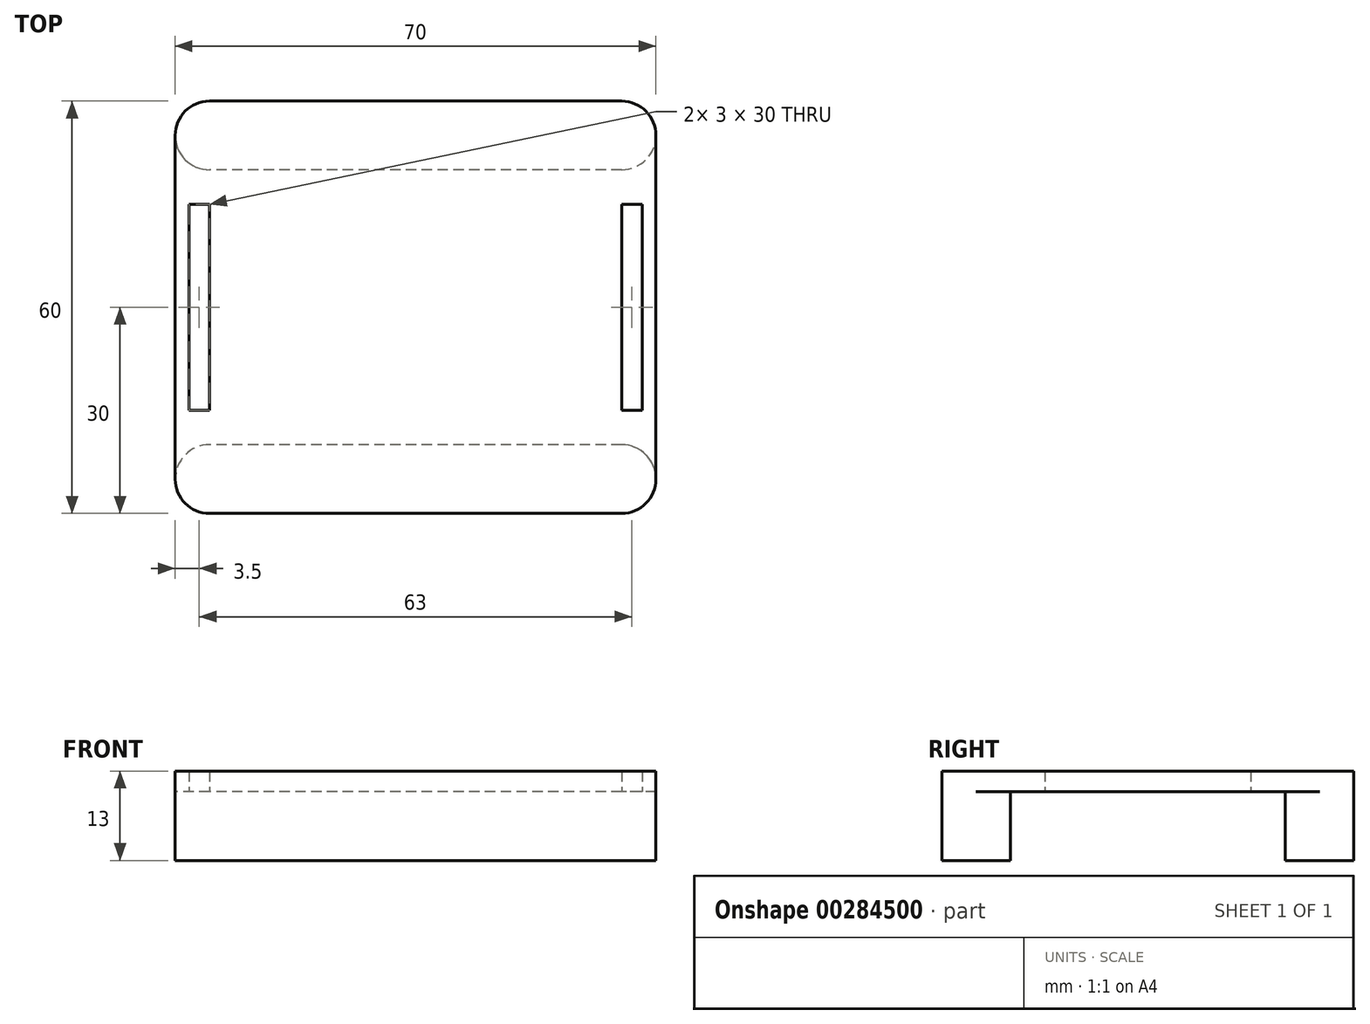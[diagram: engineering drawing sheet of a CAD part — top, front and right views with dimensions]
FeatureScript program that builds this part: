
annotation { "Feature Type Name" : "Feature", "Feature Type Description" : "" }
export const myFeature = defineFeature(function(context is Context, id is Id, definition is map)
    precondition{}
    {
        {
            var Q0;
            Q0=qCreatedBy(makeId("Top.planeOp"),FACE);
            var sketch = newSketch(context, id + "F0", { "sketchPlane" : qUnion([Q0])});
            skLineSegment(sketch, "E0.bottom", {"start": v(35, -30) * mm, "end": v(-35, -30) * mm});
            skLineSegment(sketch, "E0.top", {"start": v(35, 30) * mm, "end": v(-35, 30) * mm});
            skLineSegment(sketch, "E0.left", {"start": v(35, -30) * mm, "end": v(35, 30) * mm});
            skLineSegment(sketch, "E0.right", {"start": v(-35, -30) * mm, "end": v(-35, 30) * mm});
            skPoint(sketch, "E0.middle", {"position": v(0, 0) * mm});
            skSolve(sketch);
        }
        {
            var Q0;
            Q0 = qSketchRegion(id + "F0", true);
            extrude(context, id + "F1", {"entities" : qUnion([Q0]), "depth" : 3 * mm});
        }
        {
            var Q0;
            Q0=qCreatedBy(makeId("Top.planeOp"),FACE);
            var sketch = newSketch(context, id + "F2", { "sketchPlane" : qUnion([Q0])});
            skLineSegment(sketch, "E1.bottom", {"start": v(33, -15) * mm, "end": v(30, -15) * mm});
            skLineSegment(sketch, "E1.top", {"start": v(33, 15) * mm, "end": v(30, 15) * mm});
            skLineSegment(sketch, "E1.left", {"start": v(30, -15) * mm, "end": v(30, 15) * mm});
            skLineSegment(sketch, "E1.right", {"start": v(33, -15) * mm, "end": v(33, 15) * mm});
            skPoint(sketch, "E1.middle", {"position": v(31.5, 0) * mm});
            skLineSegment(sketch, "E2.bottom", {"start": v(-30, -15) * mm, "end": v(-33, -15) * mm});
            skLineSegment(sketch, "E2.top", {"start": v(-30, 15) * mm, "end": v(-33, 15) * mm});
            skLineSegment(sketch, "E2.left", {"start": v(-30, -15) * mm, "end": v(-30, 15) * mm});
            skLineSegment(sketch, "E2.right", {"start": v(-33, -15) * mm, "end": v(-33, 15) * mm});
            skPoint(sketch, "E2.middle", {"position": v(-31.5, 0) * mm});
            skSolve(sketch);
        }
        {
            var Q0;
            Q0 = qSketchRegion(id + "F2", true);
            extrude(context, id + "F3", {"entities" : qUnion([Q0]), "operationType" : NewBodyOperationType.REMOVE, "depth" : 25 * mm});
        }
        {
            var Q0;
            Q0=qCreatedBy(makeId("Top.planeOp"),FACE);
            var sketch = newSketch(context, id + "F4", { "sketchPlane" : qUnion([Q0])});
            skLineSegment(sketch, "E3.bottom", {"start": v(35, 20) * mm, "end": v(-35, 20) * mm});
            skLineSegment(sketch, "E3.top", {"start": v(35, 30) * mm, "end": v(-35, 30) * mm});
            skLineSegment(sketch, "E3.left", {"start": v(35, 20) * mm, "end": v(35, 30) * mm});
            skLineSegment(sketch, "E3.right", {"start": v(-35, 20) * mm, "end": v(-35, 30) * mm});
            skPoint(sketch, "E3.middle", {"position": v(0, 25) * mm});
            skLineSegment(sketch, "E4.bottom", {"start": v(35, -30) * mm, "end": v(-35, -30) * mm});
            skLineSegment(sketch, "E4.top", {"start": v(35, -20) * mm, "end": v(-35, -20) * mm});
            skLineSegment(sketch, "E4.left", {"start": v(35, -30) * mm, "end": v(35, -20) * mm});
            skLineSegment(sketch, "E4.right", {"start": v(-35, -30) * mm, "end": v(-35, -20) * mm});
            skPoint(sketch, "E4.middle", {"position": v(0, -25) * mm});
            skSolve(sketch);
        }
        {
            var Q0;
            Q0 = qSketchRegion(id + "F4", true);
            extrude(context, id + "F5", {"entities" : qUnion([Q0]), "operationType" : NewBodyOperationType.ADD, "oppositeDirection" : true, "depth" : 10 * mm});
        }
        {
            var Q0;
            Q0=makeQuery(id+"F5.boolean.opBoolean","MERGE",EDGE,{"derivedFrom":[makeQuery(id+"F1.opExtrude","SWEPT_EDGE",EDGE,{"disambiguationData":[OSD([sQuery(id+"F0.wireOp",EDGE,"E0.bottom"),sQuery(id+"F0.wireOp",EDGE,"E0.left")])]}),makeQuery(id+"F5.opExtrude","SWEPT_EDGE",EDGE,{"disambiguationData":[OSD([sQuery(id+"F4.wireOp",EDGE,"E4.bottom"),sQuery(id+"F4.wireOp",EDGE,"E4.left")])]})]});
            var Q1;
            Q1=makeQuery(id+"F5.boolean.opBoolean","MERGE",EDGE,{"derivedFrom":[makeQuery(id+"F1.opExtrude","SWEPT_EDGE",EDGE,{"disambiguationData":[OSD([sQuery(id+"F0.wireOp",EDGE,"E0.bottom"),sQuery(id+"F0.wireOp",EDGE,"E0.right")])]}),makeQuery(id+"F5.opExtrude","SWEPT_EDGE",EDGE,{"disambiguationData":[OSD([sQuery(id+"F4.wireOp",EDGE,"E4.bottom"),sQuery(id+"F4.wireOp",EDGE,"E4.right")])]})]});
            var Q2;
            Q2=makeQuery(id+"F5.opExtrude","SWEPT_EDGE",EDGE,{"disambiguationData":[OSD([sQuery(id+"F4.wireOp",EDGE,"E4.top"),sQuery(id+"F4.wireOp",EDGE,"E4.right")])]});
            var Q3;
            Q3=makeQuery(id+"F5.opExtrude","SWEPT_EDGE",EDGE,{"disambiguationData":[OSD([sQuery(id+"F4.wireOp",EDGE,"E4.top"),sQuery(id+"F4.wireOp",EDGE,"E4.left")])]});
            var Q4;
            Q4=makeQuery(id+"F5.opExtrude","SWEPT_EDGE",EDGE,{"disambiguationData":[OSD([sQuery(id+"F4.wireOp",EDGE,"E3.bottom"),sQuery(id+"F4.wireOp",EDGE,"E3.left")])]});
            var Q5;
            Q5=makeQuery(id+"F5.boolean.opBoolean","MERGE",EDGE,{"derivedFrom":[makeQuery(id+"F1.opExtrude","SWEPT_EDGE",EDGE,{"disambiguationData":[OSD([sQuery(id+"F0.wireOp",EDGE,"E0.top"),sQuery(id+"F0.wireOp",EDGE,"E0.left")])]}),makeQuery(id+"F5.opExtrude","SWEPT_EDGE",EDGE,{"disambiguationData":[OSD([sQuery(id+"F4.wireOp",EDGE,"E3.top"),sQuery(id+"F4.wireOp",EDGE,"E3.left")])]})]});
            var Q6;
            Q6=makeQuery(id+"F5.opExtrude","SWEPT_EDGE",EDGE,{"disambiguationData":[OSD([sQuery(id+"F4.wireOp",EDGE,"E3.bottom"),sQuery(id+"F4.wireOp",EDGE,"E3.right")])]});
            var Q7;
            Q7=makeQuery(id+"F5.boolean.opBoolean","MERGE",EDGE,{"derivedFrom":[makeQuery(id+"F1.opExtrude","SWEPT_EDGE",EDGE,{"disambiguationData":[OSD([sQuery(id+"F0.wireOp",EDGE,"E0.top"),sQuery(id+"F0.wireOp",EDGE,"E0.right")])]}),makeQuery(id+"F5.opExtrude","SWEPT_EDGE",EDGE,{"disambiguationData":[OSD([sQuery(id+"F4.wireOp",EDGE,"E3.top"),sQuery(id+"F4.wireOp",EDGE,"E3.right")])]})]});
            fillet(context, id + "F6", {"entities" : qUnion([Q0, Q1, Q2, Q3, Q4, Q5, Q6, Q7]), "radius" : 5 * mm, "tangentPropagation" : true, "allowEdgeOverflow" : false});
        }
    });
